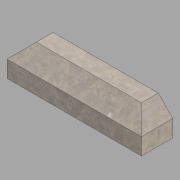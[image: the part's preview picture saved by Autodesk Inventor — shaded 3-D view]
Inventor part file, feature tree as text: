
AUTODESK INVENTOR PART (.ipt)
format: ipt  version: 2022.2 (Build 262287000, 287)  size: 135,680 bytes
history: native  units: in
note: dims shown in document units (in); Inventor stores cm internally (conversion verified against a paired STEP export)
features: extrude x2, sketch x2, mirror x1
ambient origin geometry x8: Origin, YZ Plane, XZ Plane, XY Plane, X Axis, Y Axis, Z Axis, Center Point
bodies: Solid1 (feature_tree)
feature tree (5):
  extrude  "Extrusion1"  Depth=7.5in
  extrude  "Extrusion2"  Depth=4.0in
  mirror  "Mirror1"
  sketch  "Sketch1"  dims[d0=7.5in d1=7.5in]
  sketch  "Sketch2"  dims[d2=4.0in d3=4.0in d4=3.5in d5=3.5in d6=16.0in d7=0.0in d8=3.5in d9=3.5in d10=20.0in d11=0.0in]
